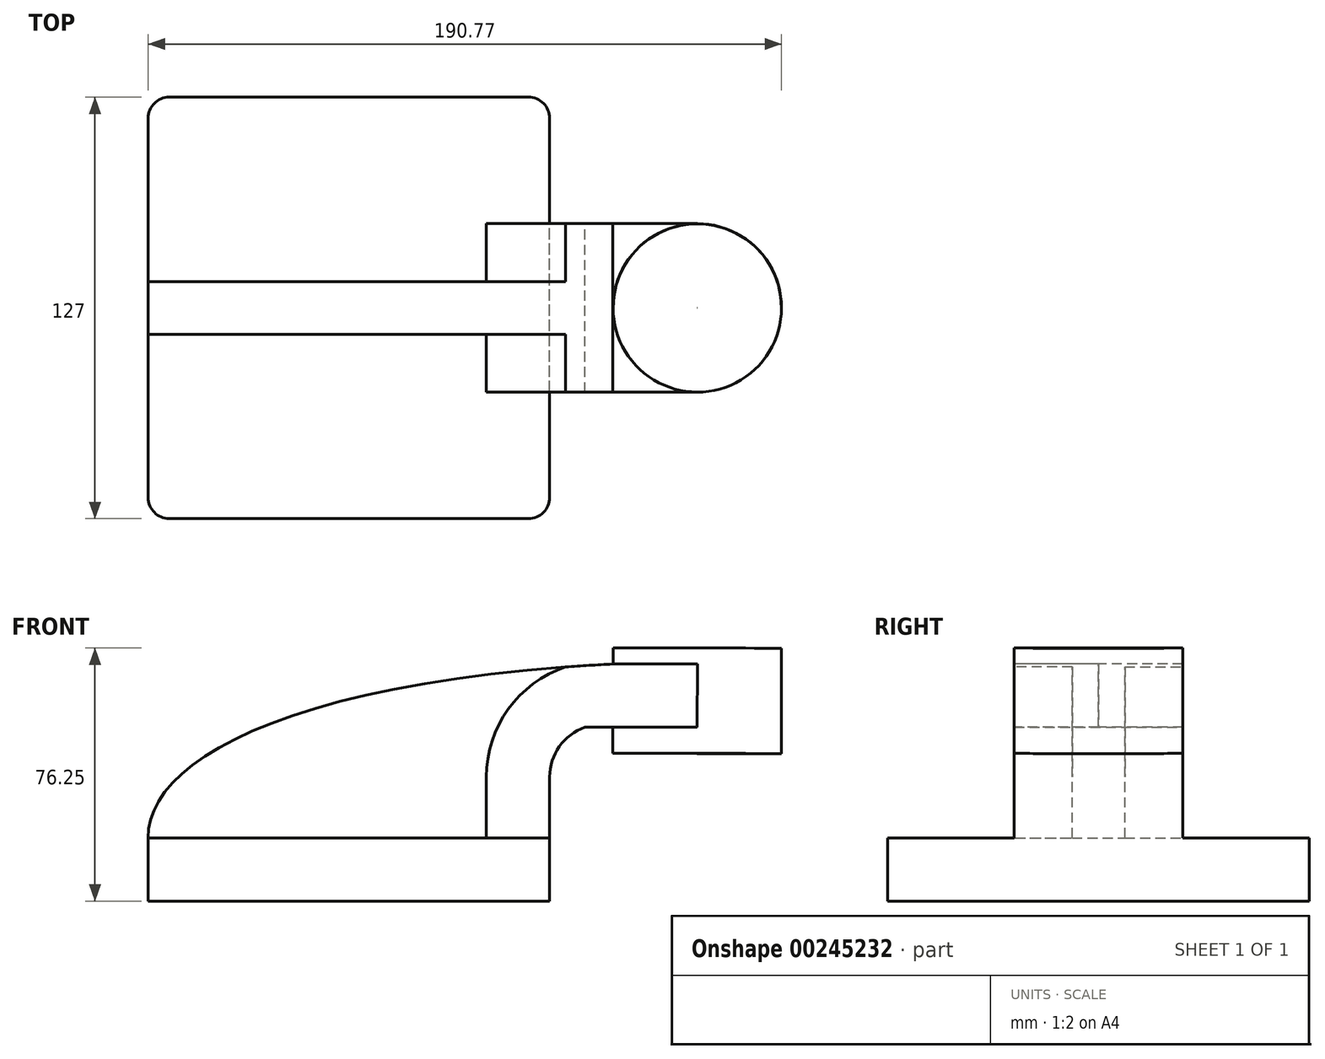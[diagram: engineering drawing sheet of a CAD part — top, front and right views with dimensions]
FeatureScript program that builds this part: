
annotation { "Feature Type Name" : "Feature", "Feature Type Description" : "" }
export const myFeature = defineFeature(function(context is Context, id is Id, definition is map)
    precondition{}
    {
        {
            var Q0;
            Q0=qCreatedBy(makeId("Front.planeOp"),FACE);
            var sketch = newSketch(context, id + "F0", { "sketchPlane" : qUnion([Q0])});
            skLineSegment(sketch, "E0.bottom", {"start": v(63.48, 9.52) * mm, "end": v(-57.43, 9.52) * mm});
            skLineSegment(sketch, "E0.top", {"start": v(63.48, -9.53) * mm, "end": v(-57.43, -9.53) * mm});
            skLineSegment(sketch, "E0.left", {"start": v(63.48, 9.52) * mm, "end": v(63.48, -9.53) * mm});
            skLineSegment(sketch, "E0.right", {"start": v(-57.43, 9.52) * mm, "end": v(-57.43, -9.53) * mm});
            skPoint(sketch, "E0.middle", {"position": v(3.02, 0) * mm});
            skLineSegment(sketch, "E1.bottom", {"start": v(133.33, 34.92) * mm, "end": v(82.53, 34.92) * mm});
            skLineSegment(sketch, "E1.top", {"start": v(133.33, 66.67) * mm, "end": v(82.53, 66.67) * mm});
            skLineSegment(sketch, "E1.left", {"start": v(133.33, 34.92) * mm, "end": v(133.33, 66.67) * mm});
            skLineSegment(sketch, "E1.right", {"start": v(82.53, 34.92) * mm, "end": v(82.53, 66.67) * mm});
            skPoint(sketch, "E1.middle", {"position": v(107.93, 50.8) * mm});
            skLineSegment(sketch, "E2", {"start": v(63.48, 9.52) * mm, "end": v(63.48, 27.86) * mm});
            skArc(sketch, "E3", {"start": v(63.48, 27.86) * mm, "mid": v(66.41, 37.05) * mm, "end": v(74.12, 42.85) * mm});
            skLineSegment(sketch, "E4", {"start": v(74.12, 42.85) * mm, "end": v(107.96, 42.85) * mm});
            skLineSegment(sketch, "E5.0", {"start": v(71.52, 61.9) * mm, "end": v(107.96, 61.9) * mm});
            skArc(sketch, "E5.1", {"start": v(44.43, 27.86) * mm, "mid": v(52.03, 49.62) * mm, "end": v(71.52, 61.9) * mm});
            skLineSegment(sketch, "E5.2", {"start": v(44.43, 9.52) * mm, "end": v(44.43, 27.86) * mm});
            skLineSegment(sketch, "E6", {"start": v(44.43, 9.52) * mm, "end": v(63.48, 9.52) * mm});
            skLineSegment(sketch, "E7", {"start": v(107.96, 61.9) * mm, "end": v(107.96, 42.85) * mm});
            skFitSpline(sketch, "E8", {"points": [v(-57.43, 9.52) * mm, v(82.53, 61.9) * mm], "startDerivative": vector(-1.5, 65.52) * mm, "endDerivative": vector(303.93, 16.1) * mm});
            skLineSegment(sketch, "E9", {"start": v(107.93, 34.92) * mm, "end": v(107.96, 66.67) * mm});
            skPoint(sketch, "E9.endSnap0", {"position": v(107.93, 66.67) * mm});
            skSolve(sketch);
        }
        {
            var Q0;
            Q0=makeQuery(id+"F0.imprint","IMPRINT",FACE,{"disambiguationData":[TD([[makeQuery(id+"F0.imprint","IMPRINT",EDGE,{"derivedFrom":sQuery(id+"F0.wireOp",EDGE,"E0.bottom")}),1.0]])]});
            extrude(context, id + "F1", {"entities" : qUnion([Q0]), "depth" : 127 * mm, "symmetric" : true});
        }
        {
            var Q0;
            Q0=makeQuery(id+"F0.imprint","IMPRINT",FACE,{"disambiguationData":[TD([[makeQuery(id+"F0.imprint","IMPRINT",EDGE,{"derivedFrom":sQuery(id+"F0.wireOp",EDGE,"E2")}),1.0]])]});
            var Q1;
            {var subQ1=sQuery(id+"F0.wireOp",EDGE,"E1.right");var subQ3=sQuery(id+"F0.wireOp",EDGE,"E4");var subQ4=makeQuery(id+"F0.imprint","INTERSECT",VERTEX,{"derivedFrom":[subQ1,subQ3]});Q1=makeQuery(id+"F0.imprint","IMPRINT",FACE,{"disambiguationData":[TD([[makeQuery(id+"F0.imprint","IMPRINT",EDGE,{"disambiguationData":[TD([[subQ4,-1.0]])],"derivedFrom":subQ3}),1.0]])]});}
            extrude(context, id + "F2", {"entities" : qUnion([Q0, Q1]), "operationType" : NewBodyOperationType.ADD, "depth" : 50.8 * mm, "symmetric" : true});
        }
        {
            var Q0;
            {var subQ0=sQuery(id+"F0.wireOp",EDGE,"E0.bottom");Q0=makeQuery(id+"F0.imprint","IMPRINT",FACE,{"disambiguationData":[TD([[makeQuery(id+"F0.imprint","IMPRINT",EDGE,{"derivedFrom":subQ0}),-1.0]])]});}
            extrude(context, id + "F3", {"entities" : qUnion([Q0]), "operationType" : NewBodyOperationType.ADD, "depth" : 15.88 * mm, "symmetric" : true});
        }
        {
            var Q0;
            {var subQ4=sQuery(id+"F0.wireOp",EDGE,"E1.left");Q0=makeQuery(id+"F0.imprint","IMPRINT",FACE,{"disambiguationData":[TD([[makeQuery(id+"F0.imprint","IMPRINT",EDGE,{"derivedFrom":subQ4}),1.0]])]});}
            var Q1;
            Q1=sQuery(id+"F0.wireOp",EDGE,"E9");
            revolve(context, id + "F4", {"operationType" : NewBodyOperationType.ADD, "entities" : qUnion([Q0]), "axis" : qUnion([Q1]), "revolveType" : RevolveType.FULL});
        }
        {
            var Q0;
            Q0=makeQuery(id+"F1.opExtrude","CAP_EDGE",EDGE,{"disambiguationData":[OSD([sQuery(id+"F0.wireOp",EDGE,"E0.left")])],"isStart":false});
            var Q1;
            Q1=makeQuery(id+"F1.opExtrude","CAP_EDGE",EDGE,{"disambiguationData":[OSD([sQuery(id+"F0.wireOp",EDGE,"E0.right")])],"isStart":false});
            var Q2;
            Q2=makeQuery(id+"F1.opExtrude","CAP_EDGE",EDGE,{"disambiguationData":[OSD([sQuery(id+"F0.wireOp",EDGE,"E0.left")])],"isStart":true});
            var Q3;
            Q3=makeQuery(id+"F1.opExtrude","CAP_EDGE",EDGE,{"disambiguationData":[OSD([sQuery(id+"F0.wireOp",EDGE,"E0.right")])],"isStart":true});
            fillet(context, id + "F5", {"entities" : qUnion([Q0, Q1, Q2, Q3]), "radius" : 6.35 * mm, "tangentPropagation" : true, "allowEdgeOverflow" : false});
        }
    });
